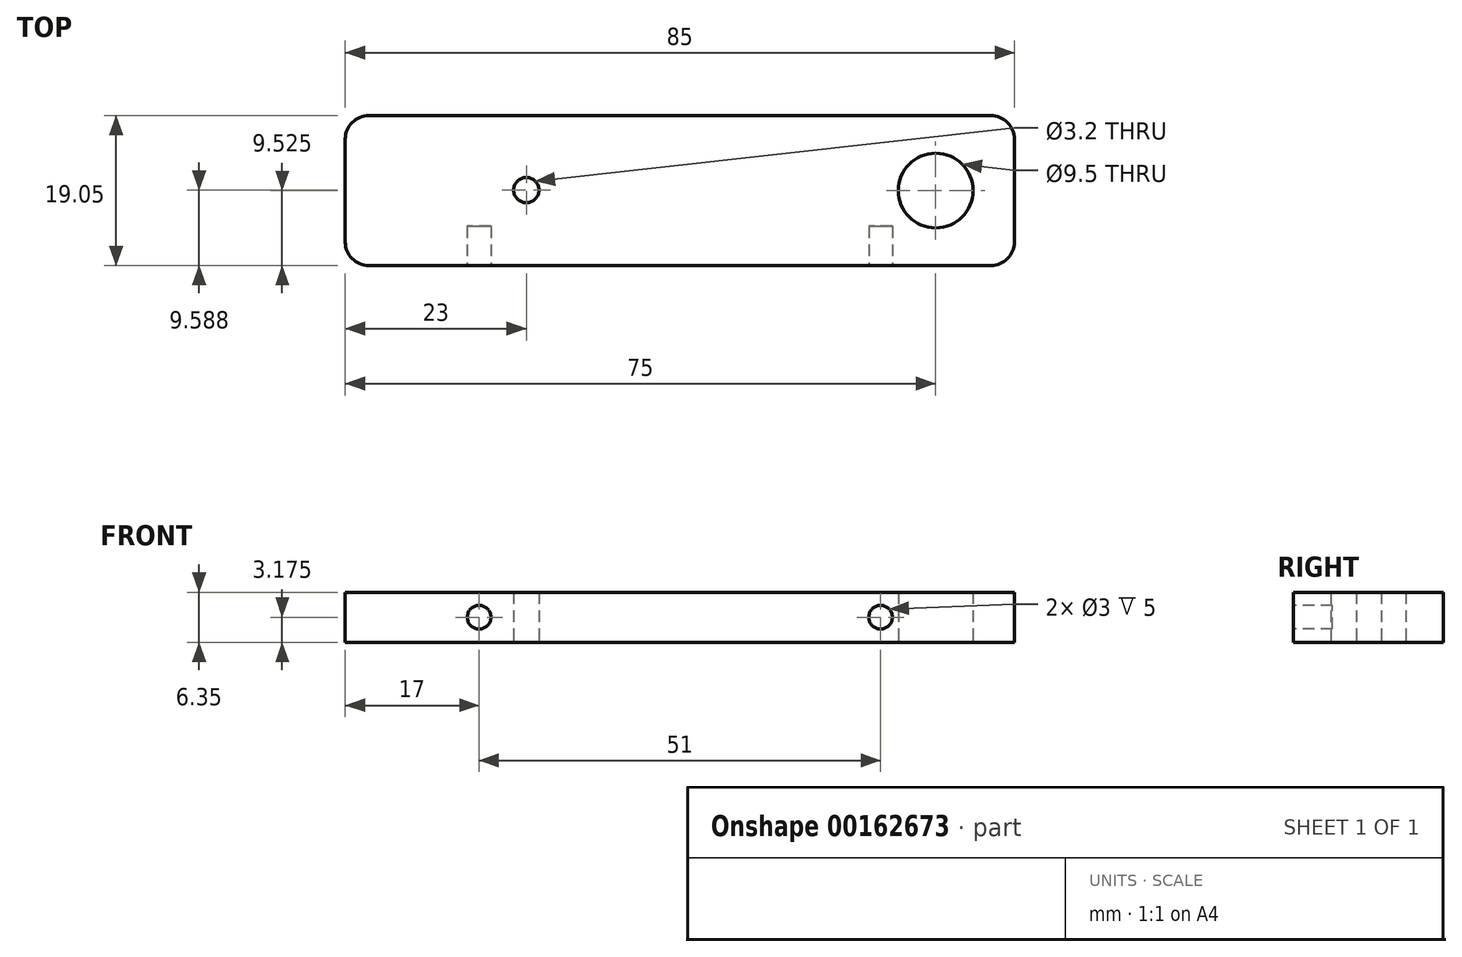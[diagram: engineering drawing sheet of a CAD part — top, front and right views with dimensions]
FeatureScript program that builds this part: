
annotation { "Feature Type Name" : "Feature", "Feature Type Description" : "" }
export const myFeature = defineFeature(function(context is Context, id is Id, definition is map)
    precondition{}
    {
        {
            var Q0;
            Q0=qCreatedBy(makeId("Top.planeOp"),FACE);
            var sketch = newSketch(context, id + "F0", { "sketchPlane" : qUnion([Q0])});
            skLineSegment(sketch, "E0.bottom", {"start": v(0, 0) * mm, "end": v(-85, 0) * mm});
            skLineSegment(sketch, "E0.top", {"start": v(0, 19.05) * mm, "end": v(-85, 19.05) * mm});
            skLineSegment(sketch, "E0.left", {"start": v(0, 0) * mm, "end": v(0, 19.05) * mm});
            skLineSegment(sketch, "E0.right", {"start": v(-85, 0) * mm, "end": v(-85, 19.05) * mm});
            skLineSegment(sketch, "E1", {"start": v(-85, 9.52) * mm, "end": v(0, 9.52) * mm, "construction": true});
            skLineSegment(sketch, "E2", {"start": v(-62, 14.65) * mm, "end": v(-62, 4.53) * mm, "construction": true});
            skLineSegment(sketch, "E3", {"start": v(-10, 14.36) * mm, "end": v(-10, 4.14) * mm, "construction": true});
            skCircle(sketch, "E4", {"center": v(-62, 9.59) * mm, "radius": 1.6 * mm});
            skCircle(sketch, "E5", {"center": v(-10, 9.52) * mm, "radius": 4.75 * mm});
            skSolve(sketch);
        }
        {
            var Q0;
            Q0 = qSketchRegion(id + "F0", true);
            extrude(context, id + "F1", {"entities" : qUnion([Q0]), "depth" : 6.35 * mm, "offsetDistance" : 25 * mm});
        }
        {
            var Q0;
            Q0=makeQuery(id+"F1.opExtrude","SWEPT_FACE",FACE,{"disambiguationData":[OSD([sQuery(id+"F0.wireOp",EDGE,"E0.bottom")])]});
            var sketch = newSketch(context, id + "F2", { "sketchPlane" : qUnion([Q0])});
            skLineSegment(sketch, "E6", {"start": v(-85, 3.17) * mm, "end": v(0, 3.17) * mm, "construction": true});
            skLineSegment(sketch, "E7", {"start": v(-68, 6.35) * mm, "end": v(-68, 0) * mm, "construction": true});
            skCircle(sketch, "E8", {"center": v(-68, 3.17) * mm, "radius": 1.5 * mm});
            skLineSegment(sketch, "E9", {"start": v(-42.5, 6.35) * mm, "end": v(-42.5, 0) * mm, "construction": true});
            skCircle(sketch, "E10.MirrorC", {"center": v(-17, 3.17) * mm, "radius": 1.5 * mm});
            skSolve(sketch);
        }
        {
            var Q0;
            Q0 = qSketchRegion(id + "F2", true);
            extrude(context, id + "F3", {"entities" : qUnion([Q0]), "operationType" : NewBodyOperationType.REMOVE, "oppositeDirection" : true, "depth" : 5 * mm, "offsetDistance" : 25 * mm});
        }
        {
            var Q0;
            Q0=makeQuery(id+"F1.opExtrude","SWEPT_EDGE",EDGE,{"disambiguationData":[OSD([sQuery(id+"F0.wireOp",EDGE,"E0.top"),sQuery(id+"F0.wireOp",EDGE,"E0.left")])]});
            var Q1;
            Q1=makeQuery(id+"F1.opExtrude","SWEPT_EDGE",EDGE,{"disambiguationData":[OSD([sQuery(id+"F0.wireOp",EDGE,"E0.top"),sQuery(id+"F0.wireOp",EDGE,"E0.right")])]});
            var Q2;
            Q2=makeQuery(id+"F1.opExtrude","SWEPT_EDGE",EDGE,{"disambiguationData":[OSD([sQuery(id+"F0.wireOp",EDGE,"E0.bottom"),sQuery(id+"F0.wireOp",EDGE,"E0.right")])]});
            var Q3;
            Q3=makeQuery(id+"F1.opExtrude","SWEPT_EDGE",EDGE,{"disambiguationData":[OSD([sQuery(id+"F0.wireOp",EDGE,"E0.bottom"),sQuery(id+"F0.wireOp",EDGE,"E0.left")])]});
            fillet(context, id + "F4", {"entities" : qUnion([Q0, Q1, Q2, Q3]), "radius" : 3 * mm, "tangentPropagation" : true, "allowEdgeOverflow" : false});
        }
    });
